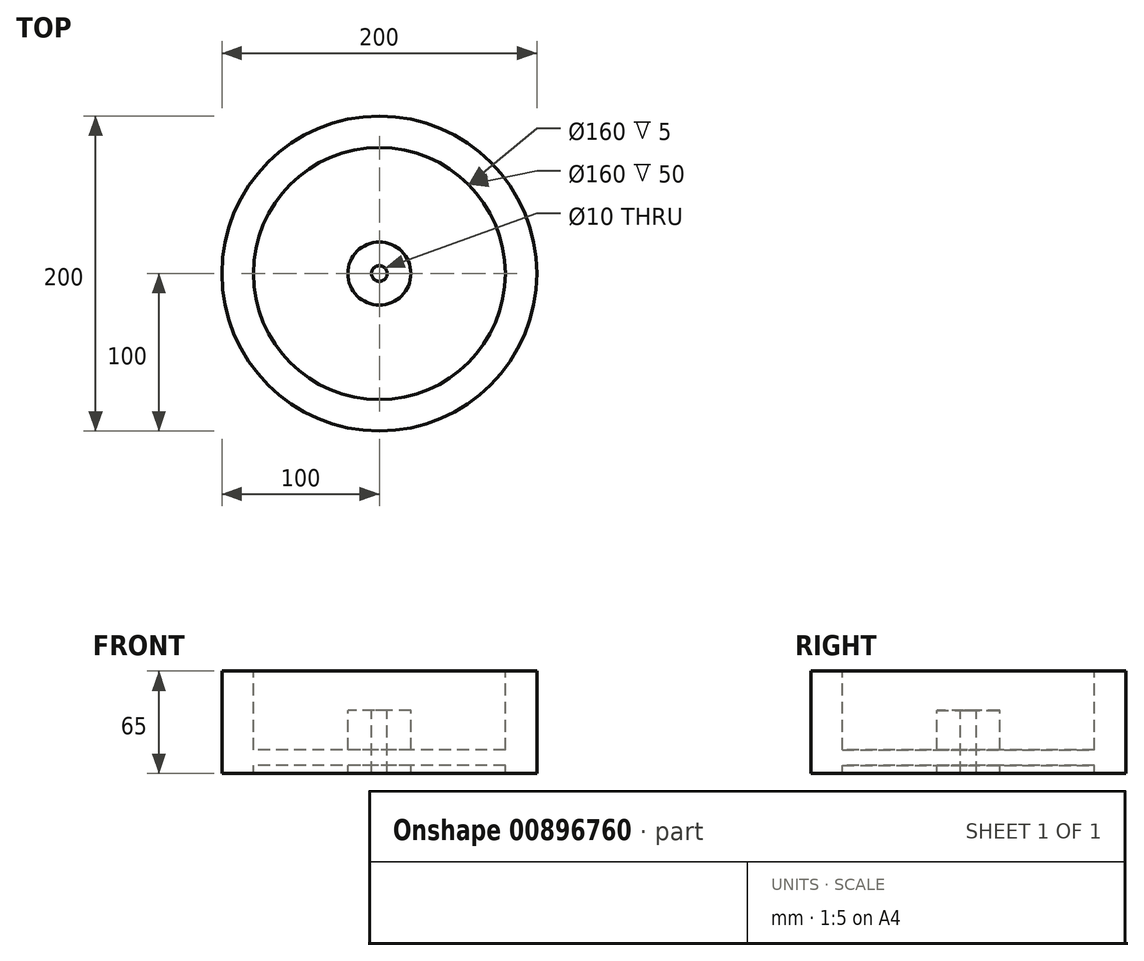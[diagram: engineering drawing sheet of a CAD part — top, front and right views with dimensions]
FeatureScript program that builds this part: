
annotation { "Feature Type Name" : "Feature", "Feature Type Description" : "" }
export const myFeature = defineFeature(function(context is Context, id is Id, definition is map)
    precondition{}
    {
        {
            var Q0;
            Q0=qCreatedBy(makeId("Front.planeOp"),FACE);
            var sketch = newSketch(context, id + "F0", { "sketchPlane" : qUnion([Q0])});
            skLineSegment(sketch, "E0", {"start": v(0, 20) * mm, "end": v(20, 20) * mm});
            skLineSegment(sketch, "E1", {"start": v(20, 20) * mm, "end": v(20, -5) * mm});
            skLineSegment(sketch, "E2", {"start": v(20, -5) * mm, "end": v(80, -5) * mm});
            skLineSegment(sketch, "E3", {"start": v(80, -5) * mm, "end": v(80, 45) * mm});
            skLineSegment(sketch, "E4", {"start": v(80, 45) * mm, "end": v(100, 45) * mm});
            skLineSegment(sketch, "E5", {"start": v(100, 45) * mm, "end": v(100, -20) * mm});
            skLineSegment(sketch, "E6", {"start": v(100, -20) * mm, "end": v(80, -20) * mm});
            skLineSegment(sketch, "E7", {"start": v(80, -20) * mm, "end": v(80, -15) * mm});
            skLineSegment(sketch, "E8", {"start": v(80, -15) * mm, "end": v(20, -15) * mm});
            skLineSegment(sketch, "E9", {"start": v(20, -15) * mm, "end": v(20, -20) * mm});
            skLineSegment(sketch, "E10", {"start": v(20, -20) * mm, "end": v(0, -20) * mm});
            skLineSegment(sketch, "E11", {"start": v(0, 20) * mm, "end": v(0, -20) * mm});
            skSolve(sketch);
        }
        {
            var Q0;
            Q0 = qSketchRegion(id + "F0", true);
            var Q1;
            Q1=sQuery(id+"F0.wireOp",EDGE,"E11");
            revolve(context, id + "F1", {"surfaceOperationType" : NewSurfaceOperationType.NEW, "entities" : qUnion([Q0]), "axis" : qUnion([Q1]), "revolveType" : RevolveType.FULL});
        }
        {
            var Q0;
            Q0=makeQuery(id+"F1.opRevolve","SWEPT_FACE",FACE,{"disambiguationData":[OSD([sQuery(id+"F0.wireOp",EDGE,"E0")])]});
            var sketch = newSketch(context, id + "F2", { "sketchPlane" : qUnion([Q0])});
            skCircle(sketch, "E12", {"center": v(0, 0) * mm, "radius": 5 * mm});
            skSolve(sketch);
        }
        {
            var Q0;
            Q0 = qSketchRegion(id + "F2", true);
            extrude(context, id + "F3", {"entities" : qUnion([Q0]), "operationType" : NewBodyOperationType.REMOVE, "endBound" : BoundingType.THROUGH_ALL, "oppositeDirection" : true, "depth" : 25 * mm, "offsetDistance" : 25 * mm});
        }
    });
